# Revit family: Halo Bench
name_source: partatom
category: Furniture
revit_build: Autodesk Revit 2015 (Build: 20150303_0715(x64)
units: mm (PartAtom-declared; Revit-internal decimal feet)

## types (28) — shared parameters
Bench Depth = 0' - 9"

## per-type parameters (varying)
| type | 18d Cushion | 21d Cushion | Arms | Bench Width | Center Leg | Cushion Array | Cushion Depth | Manufacturer | Model | No Arms | Offset | URL |
| 18dx144w | Yes | No | Yes | 12' - 0" | Yes | 16 | 1' - 3 1/2" |  |  | No | 0' - 0 3/4" |  |
| 18dx135w | Yes | No | Yes | 11' - 3" | Yes | 15 | 1' - 3 1/2" |  |  | No | 0' - 0 3/4" |  |
| 18dx126w | Yes | No | Yes | 10' - 6" | Yes | 14 | 1' - 3 1/2" |  |  | No | 0' - 0 3/4" |  |
| 18dx117w | Yes | No | Yes | 9' - 9" | Yes | 13 | 1' - 3 1/2" |  |  | No | 0' - 0 3/4" |  |
| 18dx108w | Yes | No | Yes | 9' - 0" | Yes | 12 | 1' - 3 1/2" |  |  | No | 0' - 0 3/4" |  |
| 18dx 99w | Yes | No | Yes | 8' - 3" | Yes | 11 | 1' - 3 1/2" |  |  | No | 0' - 0 3/4" |  |
| 18dx 90w | Yes | No | Yes | 7' - 6" | Yes | 10 | 1' - 3 1/2" |  |  | No | 0' - 0 3/4" |  |
| 18dx 81w | Yes | No | Yes | 6' - 9" | Yes | 9 | 1' - 3 1/2" |  |  | No | 0' - 0 3/4" |  |
| 18dx 72w | Yes | No | Yes | 6' - 0" | No | 8 | 1' - 3 1/2" |  |  | No | 0' - 0 3/4" |  |
| 18dx 63w | Yes | No | Yes | 5' - 3" | No | 7 | 1' - 3 1/2" |  |  | No | 0' - 0 3/4" |  |
| 18dx 54w | Yes | No | Yes | 4' - 6" | No | 6 | 1' - 3 1/2" |  |  | No | 0' - 0 3/4" |  |
| 18dx 45w | Yes | No | Yes | 3' - 9" | No | 5 | 1' - 3 1/2" |  |  | No | 0' - 0 3/4" |  |
| 18dx 36w | Yes | No | No | 3' - 0" | No | 4 | 1' - 3 1/2" |  |  | Yes | 0' - 1 1/2" |  |
| 18dx 27w | Yes | No | Yes | 2' - 3" | No | 3 | 1' - 3 1/2" | HALCON Furniture | Halo | No | 0' - 0 3/4" | http://www.halconfurniture.com |
| 21dx27w | No | Yes | Yes | 2' - 3" | No | 3 | 1' - 6 1/2" |  |  | No | 0' - 0 3/4" |  |
| 21dx36w | No | Yes | No | 3' - 0" | No | 4 | 1' - 6 1/2" |  |  | Yes | 0' - 1 1/2" |  |
| 21dx45w | No | Yes | Yes | 3' - 9" | No | 5 | 1' - 6 1/2" |  |  | No | 0' - 0 3/4" |  |
| 21dx54w | No | Yes | Yes | 4' - 6" | No | 6 | 1' - 6 1/2" |  |  | No | 0' - 0 3/4" |  |
| 21dx63w | No | Yes | Yes | 5' - 3" | No | 7 | 1' - 6 1/2" |  |  | No | 0' - 0 3/4" |  |
| 21dx72w | No | Yes | Yes | 6' - 0" | No | 8 | 1' - 6 1/2" |  |  | No | 0' - 0 3/4" |  |
| 21dx81w | No | Yes | Yes | 6' - 9" | Yes | 9 | 1' - 6 1/2" |  |  | No | 0' - 0 3/4" |  |
| 21dx90w | No | Yes | Yes | 7' - 6" | Yes | 10 | 1' - 6 1/2" |  |  | No | 0' - 0 3/4" |  |
| 21dx99w | No | Yes | Yes | 8' - 3" | Yes | 11 | 1' - 6 1/2" |  |  | No | 0' - 0 3/4" |  |
| 21dx108w | No | Yes | Yes | 9' - 0" | Yes | 12 | 1' - 6 1/2" |  |  | No | 0' - 0 3/4" |  |
| 21dx117w | No | Yes | Yes | 9' - 9" | Yes | 13 | 1' - 6 1/2" |  |  | No | 0' - 0 3/4" |  |
| 21dx126w | No | Yes | Yes | 10' - 6" | Yes | 14 | 1' - 6 1/2" |  |  | No | 0' - 0 3/4" |  |
| 21dx135w | No | Yes | Yes | 11' - 3" | Yes | 15 | 1' - 6 1/2" |  |  | No | 0' - 0 3/4" |  |
| 21dx144w | No | Yes | Yes | 12' - 0" | Yes | 16 | 1' - 6 1/2" | HALCON Furniture | Halo | No | 0' - 0 3/4" | http://www.halconfurniture.com |

## geometry (parser evidence)
native form markers: Sweep x5
no freeform markers — native parametric forms only
